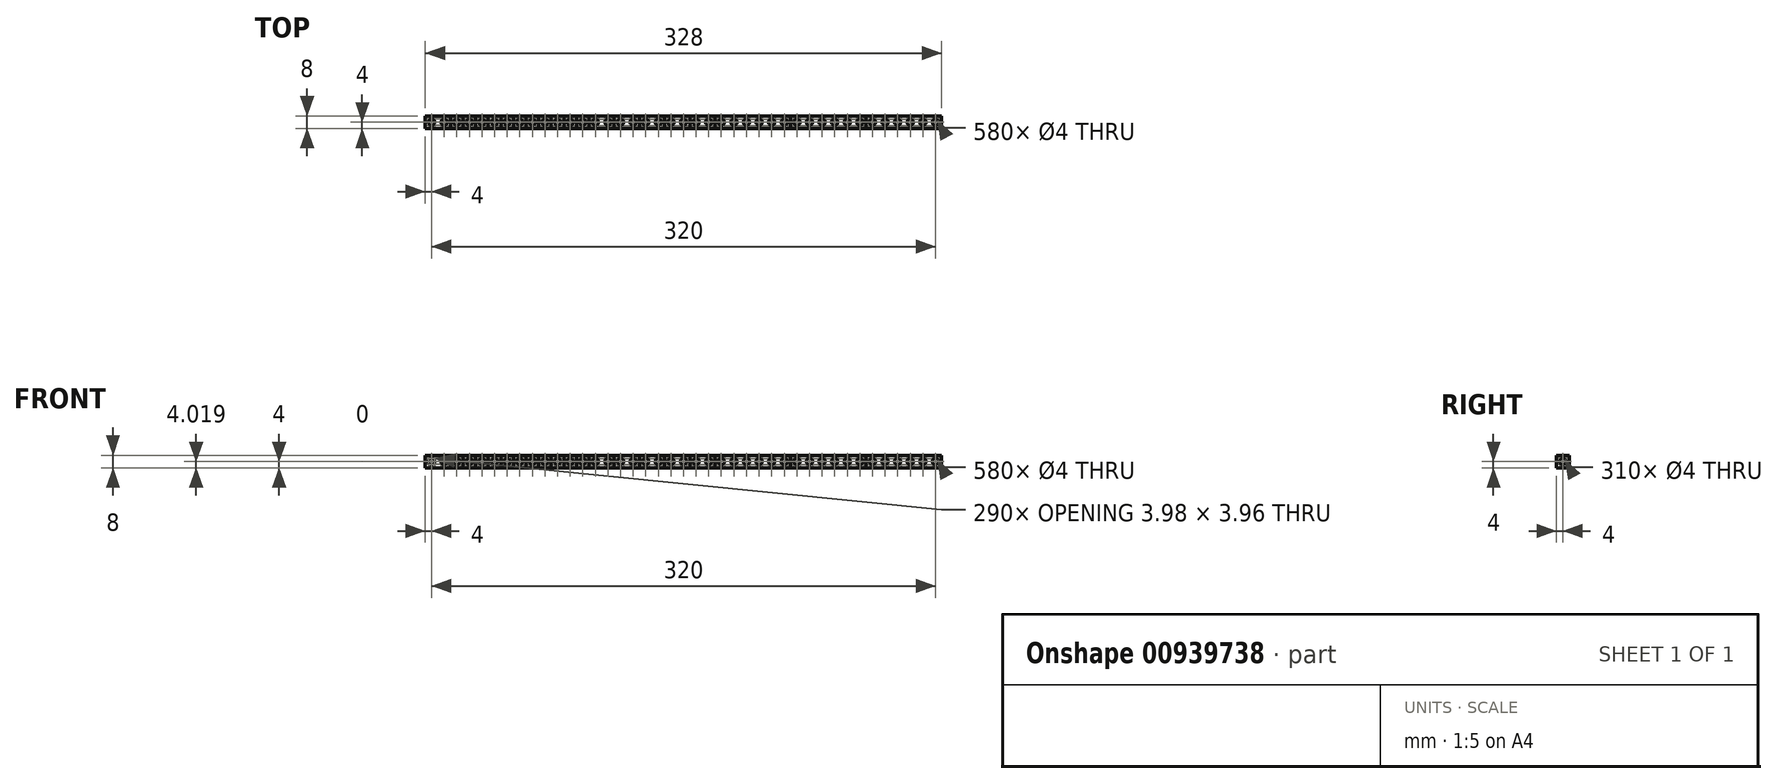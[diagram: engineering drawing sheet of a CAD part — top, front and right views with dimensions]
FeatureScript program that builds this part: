
annotation { "Feature Type Name" : "Feature", "Feature Type Description" : "" }
export const myFeature = defineFeature(function(context is Context, id is Id, definition is map)
    precondition{}
    {
        {
            var Q0;
            Q0=qCreatedBy(makeId("Right.planeOp"),FACE);
            var sketch = newSketch(context, id + "F0", { "sketchPlane" : qUnion([Q0])});
            skLineSegment(sketch, "E0.bottom", {"start": v(4, 4) * mm, "end": v(-4, 4) * mm});
            skLineSegment(sketch, "E0.top", {"start": v(4, -4) * mm, "end": v(-4, -4) * mm});
            skLineSegment(sketch, "E0.left", {"start": v(4, 4) * mm, "end": v(4, -4) * mm});
            skLineSegment(sketch, "E0.right", {"start": v(-4, 4) * mm, "end": v(-4, -4) * mm});
            skPoint(sketch, "E0.middle", {"position": v(0, 0) * mm});
            skSolve(sketch);
        }
        {
            var Q0;
            Q0=qSketchRegion(id+"F0",true);
            extrude(context, id + "F1", {"entities" : qUnion([Q0]), "depth" : 16 * mm, "offsetDistance" : 25 * mm});
        }
        {
            var Q0;
            Q0=qSketchRegion(id+"F0",true);
            extrude(context, id + "F2", {"entities" : qUnion([Q0]), "depth" : 24 * mm, "offsetDistance" : 25 * mm});
        }
        {
            var Q0;
            Q0=qSketchRegion(id+"F0",true);
            extrude(context, id + "F3", {"entities" : qUnion([Q0]), "depth" : 32 * mm, "offsetDistance" : 25 * mm});
        }
        {
            var Q0;
            Q0=qSketchRegion(id+"F0",true);
            extrude(context, id + "F4", {"entities" : qUnion([Q0]), "depth" : 40 * mm, "offsetDistance" : 25 * mm});
        }
        {
            var Q0;
            Q0=qSketchRegion(id+"F0",true);
            extrude(context, id + "F5", {"entities" : qUnion([Q0]), "depth" : 48 * mm, "offsetDistance" : 25 * mm});
        }
        {
            var Q0;
            Q0=qSketchRegion(id+"F0",true);
            extrude(context, id + "F6", {"entities" : qUnion([Q0]), "depth" : 56 * mm, "offsetDistance" : 25 * mm});
        }
        {
            var Q0;
            Q0=qSketchRegion(id+"F0",true);
            extrude(context, id + "F7", {"entities" : qUnion([Q0]), "depth" : 64 * mm, "offsetDistance" : 25 * mm});
        }
        {
            var Q0;
            Q0=qSketchRegion(id+"F0",true);
            extrude(context, id + "F8", {"entities" : qUnion([Q0]), "depth" : 72 * mm, "offsetDistance" : 25 * mm});
        }
        {
            var Q0;
            Q0=qSketchRegion(id+"F0",true);
            extrude(context, id + "F9", {"entities" : qUnion([Q0]), "depth" : 80 * mm, "offsetDistance" : 25 * mm});
        }
        {
            var Q0;
            Q0=qSketchRegion(id+"F0",true);
            extrude(context, id + "F10", {"entities" : qUnion([Q0]), "depth" : 88 * mm, "offsetDistance" : 25 * mm});
        }
        {
            var Q0;
            Q0=qSketchRegion(id+"F0",true);
            extrude(context, id + "F11", {"entities" : qUnion([Q0]), "depth" : 96 * mm, "offsetDistance" : 25 * mm});
        }
        {
            var Q0;
            Q0=qSketchRegion(id+"F0",true);
            extrude(context, id + "F12", {"entities" : qUnion([Q0]), "depth" : 104 * mm, "offsetDistance" : 25 * mm});
        }
        {
            var Q0;
            Q0=qSketchRegion(id+"F0",true);
            extrude(context, id + "F13", {"entities" : qUnion([Q0]), "depth" : 120 * mm, "offsetDistance" : 25 * mm});
        }
        {
            var Q0;
            Q0=qSketchRegion(id+"F0",true);
            extrude(context, id + "F14", {"entities" : qUnion([Q0]), "depth" : 136 * mm, "offsetDistance" : 25 * mm});
        }
        {
            var Q0;
            Q0=qSketchRegion(id+"F0",true);
            extrude(context, id + "F15", {"entities" : qUnion([Q0]), "depth" : 152 * mm, "offsetDistance" : 25 * mm});
        }
        {
            var Q0;
            Q0=qSketchRegion(id+"F0",true);
            extrude(context, id + "F16", {"entities" : qUnion([Q0]), "depth" : 168 * mm, "offsetDistance" : 25 * mm});
        }
        {
            var Q0;
            Q0=qSketchRegion(id+"F0",true);
            extrude(context, id + "F17", {"entities" : qUnion([Q0]), "depth" : 184 * mm, "offsetDistance" : 25 * mm});
        }
        {
            var Q0;
            Q0=qSketchRegion(id+"F0",true);
            extrude(context, id + "F18", {"entities" : qUnion([Q0]), "depth" : 232 * mm, "offsetDistance" : 25 * mm});
        }
        {
            var Q0;
            Q0=qSketchRegion(id+"F0",true);
            extrude(context, id + "F19", {"entities" : qUnion([Q0]), "depth" : 280 * mm, "offsetDistance" : 25 * mm});
        }
        {
            var Q0;
            Q0=qSketchRegion(id+"F0",true);
            extrude(context, id + "F20", {"entities" : qUnion([Q0]), "depth" : 328 * mm, "offsetDistance" : 25 * mm});
        }
        {
            var Q0;
            Q0=qCreatedBy(makeId("Front.planeOp"),FACE);
            var sketch = newSketch(context, id + "F21", { "sketchPlane" : qUnion([Q0])});
            skCircle(sketch, "E1", {"center": v(4, 0) * mm, "radius": 2 * mm});
            skCircle(sketch, "E2.1.0.0", {"center": v(12, 0) * mm, "radius": 2 * mm});
            skCircle(sketch, "E2.2.0.0", {"center": v(20, 0) * mm, "radius": 2 * mm});
            skCircle(sketch, "E2.3.0.0", {"center": v(28, 0) * mm, "radius": 2 * mm});
            skCircle(sketch, "E2.4.0.0", {"center": v(36, 0) * mm, "radius": 2 * mm});
            skCircle(sketch, "E2.5.0.0", {"center": v(44, 0) * mm, "radius": 2 * mm});
            skCircle(sketch, "E2.6.0.0", {"center": v(52, 0) * mm, "radius": 2 * mm});
            skCircle(sketch, "E2.7.0.0", {"center": v(60, 0) * mm, "radius": 2 * mm});
            skCircle(sketch, "E2.8.0.0", {"center": v(68, 0) * mm, "radius": 2 * mm});
            skCircle(sketch, "E2.9.0.0", {"center": v(76, 0) * mm, "radius": 2 * mm});
            skCircle(sketch, "E2.10.0.0", {"center": v(84, 0) * mm, "radius": 2 * mm});
            skCircle(sketch, "E2.11.0.0", {"center": v(92, 0) * mm, "radius": 2 * mm});
            skCircle(sketch, "E2.12.0.0", {"center": v(100, 0) * mm, "radius": 2 * mm});
            skCircle(sketch, "E2.13.0.0", {"center": v(108, 0) * mm, "radius": 2 * mm});
            skCircle(sketch, "E2.14.0.0", {"center": v(116, 0) * mm, "radius": 2 * mm});
            skCircle(sketch, "E2.15.0.0", {"center": v(124, 0) * mm, "radius": 2 * mm});
            skCircle(sketch, "E2.16.0.0", {"center": v(132, 0) * mm, "radius": 2 * mm});
            skCircle(sketch, "E2.17.0.0", {"center": v(140, 0) * mm, "radius": 2 * mm});
            skCircle(sketch, "E2.18.0.0", {"center": v(148, 0) * mm, "radius": 2 * mm});
            skCircle(sketch, "E2.19.0.0", {"center": v(156, 0) * mm, "radius": 2 * mm});
            skCircle(sketch, "E2.20.0.0", {"center": v(164, 0) * mm, "radius": 2 * mm});
            skCircle(sketch, "E2.21.0.0", {"center": v(172, 0) * mm, "radius": 2 * mm});
            skCircle(sketch, "E2.22.0.0", {"center": v(180, 0) * mm, "radius": 2 * mm});
            skCircle(sketch, "E2.23.0.0", {"center": v(188, 0) * mm, "radius": 2 * mm});
            skCircle(sketch, "E2.24.0.0", {"center": v(196, 0) * mm, "radius": 2 * mm});
            skCircle(sketch, "E2.25.0.0", {"center": v(204, 0) * mm, "radius": 2 * mm});
            skCircle(sketch, "E2.26.0.0", {"center": v(212, 0) * mm, "radius": 2 * mm});
            skCircle(sketch, "E2.27.0.0", {"center": v(220, 0) * mm, "radius": 2 * mm});
            skCircle(sketch, "E2.28.0.0", {"center": v(228, 0) * mm, "radius": 2 * mm});
            skCircle(sketch, "E2.29.0.0", {"center": v(236, 0) * mm, "radius": 2 * mm});
            skCircle(sketch, "E2.30.0.0", {"center": v(244, 0) * mm, "radius": 2 * mm});
            skCircle(sketch, "E2.31.0.0", {"center": v(252, 0) * mm, "radius": 2 * mm});
            skCircle(sketch, "E2.32.0.0", {"center": v(260, 0) * mm, "radius": 2 * mm});
            skCircle(sketch, "E2.33.0.0", {"center": v(268, 0) * mm, "radius": 2 * mm});
            skCircle(sketch, "E2.34.0.0", {"center": v(276, 0) * mm, "radius": 2 * mm});
            skCircle(sketch, "E2.35.0.0", {"center": v(284, 0) * mm, "radius": 2 * mm});
            skCircle(sketch, "E2.36.0.0", {"center": v(292, 0) * mm, "radius": 2 * mm});
            skCircle(sketch, "E2.37.0.0", {"center": v(300, 0) * mm, "radius": 2 * mm});
            skCircle(sketch, "E2.38.0.0", {"center": v(308, 0) * mm, "radius": 2 * mm});
            skCircle(sketch, "E2.39.0.0", {"center": v(316, 0) * mm, "radius": 2 * mm});
            skCircle(sketch, "E2.40.0.0", {"center": v(324, 0) * mm, "radius": 2 * mm});
            skLineSegment(sketch, "E2.direction1", {"start": v(4, 0) * mm, "end": v(12, 0) * mm, "construction": true});
            skSolve(sketch);
        }
        {
            var Q0;
            Q0=qSketchRegion(id+"F21",true);
            extrude(context, id + "F22", {"entities" : qUnion([Q0]), "operationType" : NewBodyOperationType.REMOVE, "oppositeDirection" : true, "depth" : 25 * mm, "offsetDistance" : 25 * mm, "symmetric" : true});
        }
        {
            var Q0;
            Q0=qCreatedBy(makeId("Top.planeOp"),FACE);
            var sketch = newSketch(context, id + "F23", { "sketchPlane" : qUnion([Q0])});
            skCircle(sketch, "E3", {"center": v(4, 0) * mm, "radius": 2 * mm});
            skCircle(sketch, "E4.1.0.0", {"center": v(12, 0) * mm, "radius": 2 * mm});
            skCircle(sketch, "E4.2.0.0", {"center": v(20, 0) * mm, "radius": 2 * mm});
            skCircle(sketch, "E4.3.0.0", {"center": v(28, 0) * mm, "radius": 2 * mm});
            skCircle(sketch, "E4.4.0.0", {"center": v(36, 0) * mm, "radius": 2 * mm});
            skCircle(sketch, "E4.5.0.0", {"center": v(44, 0) * mm, "radius": 2 * mm});
            skCircle(sketch, "E4.6.0.0", {"center": v(52, 0) * mm, "radius": 2 * mm});
            skCircle(sketch, "E4.7.0.0", {"center": v(60, 0) * mm, "radius": 2 * mm});
            skCircle(sketch, "E4.8.0.0", {"center": v(68, 0) * mm, "radius": 2 * mm});
            skCircle(sketch, "E4.9.0.0", {"center": v(76, 0) * mm, "radius": 2 * mm});
            skCircle(sketch, "E4.10.0.0", {"center": v(84, 0) * mm, "radius": 2 * mm});
            skCircle(sketch, "E4.11.0.0", {"center": v(92, 0) * mm, "radius": 2 * mm});
            skCircle(sketch, "E4.12.0.0", {"center": v(100, 0) * mm, "radius": 2 * mm});
            skCircle(sketch, "E4.13.0.0", {"center": v(108, 0) * mm, "radius": 2 * mm});
            skCircle(sketch, "E4.14.0.0", {"center": v(116, 0) * mm, "radius": 2 * mm});
            skCircle(sketch, "E4.15.0.0", {"center": v(124, 0) * mm, "radius": 2 * mm});
            skCircle(sketch, "E4.16.0.0", {"center": v(132, 0) * mm, "radius": 2 * mm});
            skCircle(sketch, "E4.17.0.0", {"center": v(140, 0) * mm, "radius": 2 * mm});
            skCircle(sketch, "E4.18.0.0", {"center": v(148, 0) * mm, "radius": 2 * mm});
            skCircle(sketch, "E4.19.0.0", {"center": v(156, 0) * mm, "radius": 2 * mm});
            skCircle(sketch, "E4.20.0.0", {"center": v(164, 0) * mm, "radius": 2 * mm});
            skCircle(sketch, "E4.21.0.0", {"center": v(172, 0) * mm, "radius": 2 * mm});
            skCircle(sketch, "E4.22.0.0", {"center": v(180, 0) * mm, "radius": 2 * mm});
            skCircle(sketch, "E4.23.0.0", {"center": v(188, 0) * mm, "radius": 2 * mm});
            skCircle(sketch, "E4.24.0.0", {"center": v(196, 0) * mm, "radius": 2 * mm});
            skCircle(sketch, "E4.25.0.0", {"center": v(204, 0) * mm, "radius": 2 * mm});
            skCircle(sketch, "E4.26.0.0", {"center": v(212, 0) * mm, "radius": 2 * mm});
            skCircle(sketch, "E4.27.0.0", {"center": v(220, 0) * mm, "radius": 2 * mm});
            skCircle(sketch, "E4.28.0.0", {"center": v(228, 0) * mm, "radius": 2 * mm});
            skCircle(sketch, "E4.29.0.0", {"center": v(236, 0) * mm, "radius": 2 * mm});
            skCircle(sketch, "E4.30.0.0", {"center": v(244, 0) * mm, "radius": 2 * mm});
            skCircle(sketch, "E4.31.0.0", {"center": v(252, 0) * mm, "radius": 2 * mm});
            skCircle(sketch, "E4.32.0.0", {"center": v(260, 0) * mm, "radius": 2 * mm});
            skCircle(sketch, "E4.33.0.0", {"center": v(268, 0) * mm, "radius": 2 * mm});
            skCircle(sketch, "E4.34.0.0", {"center": v(276, 0) * mm, "radius": 2 * mm});
            skCircle(sketch, "E4.35.0.0", {"center": v(284, 0) * mm, "radius": 2 * mm});
            skCircle(sketch, "E4.36.0.0", {"center": v(292, 0) * mm, "radius": 2 * mm});
            skCircle(sketch, "E4.37.0.0", {"center": v(300, 0) * mm, "radius": 2 * mm});
            skCircle(sketch, "E4.38.0.0", {"center": v(308, 0) * mm, "radius": 2 * mm});
            skCircle(sketch, "E4.39.0.0", {"center": v(316, 0) * mm, "radius": 2 * mm});
            skCircle(sketch, "E4.40.0.0", {"center": v(324, 0) * mm, "radius": 2 * mm});
            skLineSegment(sketch, "E4.direction1", {"start": v(4, 0) * mm, "end": v(12, 0) * mm, "construction": true});
            skSolve(sketch);
        }
        {
            var Q0;
            Q0=qSketchRegion(id+"F23",true);
            extrude(context, id + "F24", {"entities" : qUnion([Q0]), "operationType" : NewBodyOperationType.REMOVE, "depth" : 25 * mm, "offsetDistance" : 25 * mm, "symmetric" : true});
        }
        {
            var Q0;
            Q0=qCreatedBy(makeId("Right.planeOp"),FACE);
            var sketch = newSketch(context, id + "F25", { "sketchPlane" : qUnion([Q0])});
            skCircle(sketch, "E5", {"center": v(0, 0) * mm, "radius": 2 * mm});
            skSolve(sketch);
        }
        {
            var Q0;
            Q0=qSketchRegion(id+"F25",true);
            extrude(context, id + "F26", {"entities" : qUnion([Q0]), "operationType" : NewBodyOperationType.REMOVE, "depth" : 12 * mm, "offsetDistance" : 25 * mm});
        }
        {
            var Q0;
            Q0=qCreatedBy(makeId("Right.planeOp"),FACE);
            cPlane(context, id + "F27", {"entities" : qUnion([Q0]), "cplaneType" : CPlaneType.OFFSET, "offset" : 328 * mm, "width" : 150 * mm, "height" : 150 * mm});
        }
        {
            var Q0;
            Q0=qCreatedBy(id+"F27.planeOp",FACE);
            var sketch = newSketch(context, id + "F28", { "sketchPlane" : qUnion([Q0])});
            skCircle(sketch, "E6", {"center": v(0, 0) * mm, "radius": 2 * mm});
            skSolve(sketch);
        }
        {
            var Q0;
            Q0=qSketchRegion(id+"F28",true);
            var Q1;
            {var subQ0=makeQuery(id+"F24.opExtrude","SWEPT_FACE",FACE,{"disambiguationData":[OSD([sQuery(id+"F23.wireOp",EDGE,"E4.1.0.0")])]});Q1=makeQuery(id+"F24.boolean.opBoolean","COPY",FACE,{"disambiguationData":[TD([makeQuery(id+"F1.opExtrude","SWEPT_FACE",FACE,{"disambiguationData":[OSD([sQuery(id+"F0.wireOp",EDGE,"E0.top")])]})])],"derivedFrom":subQ0});}
            extrude(context, id + "F29", {"entities" : qUnion([Q0]), "operationType" : NewBodyOperationType.REMOVE, "endBound" : BoundingType.UP_TO_SURFACE, "oppositeDirection" : true, "depth" : 25 * mm, "endBoundEntityFace" : qUnion([Q1]), "offsetDistance" : 25 * mm});
        }
        {
            var Q0;
            Q0=qSketchRegion(id+"F28",true);
            var Q1;
            {var subQ0=makeQuery(id+"F24.opExtrude","SWEPT_FACE",FACE,{"disambiguationData":[OSD([sQuery(id+"F23.wireOp",EDGE,"E4.1.0.0")])]});Q1=makeQuery(id+"F24.boolean.opBoolean","COPY",FACE,{"disambiguationData":[TD([makeQuery(id+"F1.opExtrude","SWEPT_FACE",FACE,{"disambiguationData":[OSD([sQuery(id+"F0.wireOp",EDGE,"E0.top")])]})])],"derivedFrom":subQ0});}
            extrude(context, id + "F30", {"entities" : qUnion([Q0]), "operationType" : NewBodyOperationType.REMOVE, "endBound" : BoundingType.UP_TO_SURFACE, "oppositeDirection" : true, "depth" : 25 * mm, "endBoundEntityFace" : qUnion([Q1]), "offsetDistance" : 25 * mm});
        }
        {
            var Q0;
            Q0=qSketchRegion(id+"F28",true);
            var Q1;
            {var subQ0=makeQuery(id+"F24.opExtrude","SWEPT_FACE",FACE,{"disambiguationData":[OSD([sQuery(id+"F23.wireOp",EDGE,"E4.2.0.0")])]});Q1=makeQuery(id+"F24.boolean.opBoolean","COPY",FACE,{"disambiguationData":[TD([makeQuery(id+"F2.opExtrude","SWEPT_FACE",FACE,{"disambiguationData":[OSD([sQuery(id+"F0.wireOp",EDGE,"E0.top")])]})])],"derivedFrom":subQ0});}
            extrude(context, id + "F31", {"entities" : qUnion([Q0]), "operationType" : NewBodyOperationType.REMOVE, "endBound" : BoundingType.UP_TO_SURFACE, "oppositeDirection" : true, "depth" : 25 * mm, "endBoundEntityFace" : qUnion([Q1]), "offsetDistance" : 25 * mm});
        }
        {
            var Q0;
            Q0=qSketchRegion(id+"F28",true);
            var Q1;
            {var subQ0=makeQuery(id+"F24.opExtrude","SWEPT_FACE",FACE,{"disambiguationData":[OSD([sQuery(id+"F23.wireOp",EDGE,"E4.3.0.0")])]});Q1=makeQuery(id+"F24.boolean.opBoolean","COPY",FACE,{"disambiguationData":[TD([makeQuery(id+"F3.opExtrude","SWEPT_FACE",FACE,{"disambiguationData":[OSD([sQuery(id+"F0.wireOp",EDGE,"E0.top")])]})])],"derivedFrom":subQ0});}
            extrude(context, id + "F32", {"entities" : qUnion([Q0]), "operationType" : NewBodyOperationType.REMOVE, "endBound" : BoundingType.UP_TO_SURFACE, "oppositeDirection" : true, "depth" : 25 * mm, "endBoundEntityFace" : qUnion([Q1]), "offsetDistance" : 25 * mm});
        }
        {
            var Q0;
            Q0=qSketchRegion(id+"F28",true);
            var Q1;
            {var subQ0=makeQuery(id+"F24.opExtrude","SWEPT_FACE",FACE,{"disambiguationData":[OSD([sQuery(id+"F23.wireOp",EDGE,"E4.4.0.0")])]});Q1=makeQuery(id+"F24.boolean.opBoolean","COPY",FACE,{"disambiguationData":[TD([makeQuery(id+"F5.opExtrude","SWEPT_FACE",FACE,{"disambiguationData":[OSD([sQuery(id+"F0.wireOp",EDGE,"E0.top")])]})])],"derivedFrom":subQ0});}
            extrude(context, id + "F33", {"entities" : qUnion([Q0]), "operationType" : NewBodyOperationType.REMOVE, "endBound" : BoundingType.UP_TO_SURFACE, "oppositeDirection" : true, "depth" : 25 * mm, "endBoundEntityFace" : qUnion([Q1]), "offsetDistance" : 25 * mm});
        }
        {
            var Q0;
            Q0=qSketchRegion(id+"F28",true);
            var Q1;
            {var subQ0=makeQuery(id+"F24.opExtrude","SWEPT_FACE",FACE,{"disambiguationData":[OSD([sQuery(id+"F23.wireOp",EDGE,"E4.5.0.0")])]});Q1=makeQuery(id+"F24.boolean.opBoolean","COPY",FACE,{"disambiguationData":[TD([makeQuery(id+"F6.opExtrude","SWEPT_FACE",FACE,{"disambiguationData":[OSD([sQuery(id+"F0.wireOp",EDGE,"E0.top")])]})])],"derivedFrom":subQ0});}
            extrude(context, id + "F34", {"entities" : qUnion([Q0]), "operationType" : NewBodyOperationType.REMOVE, "endBound" : BoundingType.UP_TO_SURFACE, "oppositeDirection" : true, "depth" : 25 * mm, "endBoundEntityFace" : qUnion([Q1]), "offsetDistance" : 25 * mm});
        }
        {
            var Q0;
            Q0=qSketchRegion(id+"F28",true);
            var Q1;
            {var subQ0=makeQuery(id+"F24.opExtrude","SWEPT_FACE",FACE,{"disambiguationData":[OSD([sQuery(id+"F23.wireOp",EDGE,"E4.6.0.0")])]});Q1=makeQuery(id+"F24.boolean.opBoolean","COPY",FACE,{"disambiguationData":[TD([makeQuery(id+"F7.opExtrude","SWEPT_FACE",FACE,{"disambiguationData":[OSD([sQuery(id+"F0.wireOp",EDGE,"E0.top")])]})])],"derivedFrom":subQ0});}
            extrude(context, id + "F35", {"entities" : qUnion([Q0]), "operationType" : NewBodyOperationType.REMOVE, "endBound" : BoundingType.UP_TO_SURFACE, "oppositeDirection" : true, "depth" : 25 * mm, "endBoundEntityFace" : qUnion([Q1]), "offsetDistance" : 25 * mm});
        }
        {
            var Q0;
            Q0=qSketchRegion(id+"F28",true);
            var Q1;
            {var subQ0=makeQuery(id+"F24.opExtrude","SWEPT_FACE",FACE,{"disambiguationData":[OSD([sQuery(id+"F23.wireOp",EDGE,"E4.7.0.0")])]});Q1=makeQuery(id+"F24.boolean.opBoolean","COPY",FACE,{"disambiguationData":[TD([makeQuery(id+"F8.opExtrude","SWEPT_FACE",FACE,{"disambiguationData":[OSD([sQuery(id+"F0.wireOp",EDGE,"E0.top")])]})])],"derivedFrom":subQ0});}
            extrude(context, id + "F36", {"entities" : qUnion([Q0]), "operationType" : NewBodyOperationType.REMOVE, "endBound" : BoundingType.UP_TO_SURFACE, "oppositeDirection" : true, "depth" : 25 * mm, "endBoundEntityFace" : qUnion([Q1]), "offsetDistance" : 25 * mm});
        }
        {
            var Q0;
            Q0=qSketchRegion(id+"F28",true);
            var Q1;
            {var subQ0=makeQuery(id+"F24.opExtrude","SWEPT_FACE",FACE,{"disambiguationData":[OSD([sQuery(id+"F23.wireOp",EDGE,"E4.8.0.0")])]});Q1=makeQuery(id+"F24.boolean.opBoolean","COPY",FACE,{"disambiguationData":[TD([makeQuery(id+"F9.opExtrude","SWEPT_FACE",FACE,{"disambiguationData":[OSD([sQuery(id+"F0.wireOp",EDGE,"E0.top")])]})])],"derivedFrom":subQ0});}
            extrude(context, id + "F37", {"entities" : qUnion([Q0]), "operationType" : NewBodyOperationType.REMOVE, "endBound" : BoundingType.UP_TO_SURFACE, "oppositeDirection" : true, "depth" : 25 * mm, "endBoundEntityFace" : qUnion([Q1]), "offsetDistance" : 25 * mm});
        }
        {
            var Q0;
            Q0=qSketchRegion(id+"F28",true);
            var Q1;
            {var subQ0=makeQuery(id+"F24.opExtrude","SWEPT_FACE",FACE,{"disambiguationData":[OSD([sQuery(id+"F23.wireOp",EDGE,"E4.9.0.0")])]});Q1=makeQuery(id+"F24.boolean.opBoolean","COPY",FACE,{"disambiguationData":[TD([makeQuery(id+"F10.opExtrude","SWEPT_FACE",FACE,{"disambiguationData":[OSD([sQuery(id+"F0.wireOp",EDGE,"E0.top")])]})])],"derivedFrom":subQ0});}
            extrude(context, id + "F38", {"entities" : qUnion([Q0]), "operationType" : NewBodyOperationType.REMOVE, "endBound" : BoundingType.UP_TO_SURFACE, "oppositeDirection" : true, "depth" : 25 * mm, "endBoundEntityFace" : qUnion([Q1]), "offsetDistance" : 25 * mm});
        }
        {
            var Q0;
            Q0=qSketchRegion(id+"F28",true);
            var Q1;
            {var subQ0=makeQuery(id+"F24.opExtrude","SWEPT_FACE",FACE,{"disambiguationData":[OSD([sQuery(id+"F23.wireOp",EDGE,"E4.10.0.0")])]});Q1=makeQuery(id+"F24.boolean.opBoolean","COPY",FACE,{"disambiguationData":[TD([makeQuery(id+"F11.opExtrude","SWEPT_FACE",FACE,{"disambiguationData":[OSD([sQuery(id+"F0.wireOp",EDGE,"E0.top")])]})])],"derivedFrom":subQ0});}
            extrude(context, id + "F39", {"entities" : qUnion([Q0]), "operationType" : NewBodyOperationType.REMOVE, "endBound" : BoundingType.UP_TO_SURFACE, "oppositeDirection" : true, "depth" : 25 * mm, "endBoundEntityFace" : qUnion([Q1]), "offsetDistance" : 25 * mm});
        }
        {
            var Q0;
            Q0=qSketchRegion(id+"F28",true);
            var Q1;
            {var subQ0=makeQuery(id+"F24.opExtrude","SWEPT_FACE",FACE,{"disambiguationData":[OSD([sQuery(id+"F23.wireOp",EDGE,"E4.11.0.0")])]});Q1=makeQuery(id+"F24.boolean.opBoolean","COPY",FACE,{"disambiguationData":[TD([makeQuery(id+"F12.opExtrude","SWEPT_FACE",FACE,{"disambiguationData":[OSD([sQuery(id+"F0.wireOp",EDGE,"E0.top")])]})])],"derivedFrom":subQ0});}
            extrude(context, id + "F40", {"entities" : qUnion([Q0]), "operationType" : NewBodyOperationType.REMOVE, "endBound" : BoundingType.UP_TO_SURFACE, "oppositeDirection" : true, "depth" : 25 * mm, "endBoundEntityFace" : qUnion([Q1]), "offsetDistance" : 25 * mm});
        }
        {
            var Q0;
            Q0=qSketchRegion(id+"F28",true);
            var Q1;
            {var subQ0=makeQuery(id+"F24.opExtrude","SWEPT_FACE",FACE,{"disambiguationData":[OSD([sQuery(id+"F23.wireOp",EDGE,"E4.13.0.0")])]});Q1=makeQuery(id+"F24.boolean.opBoolean","COPY",FACE,{"disambiguationData":[TD([makeQuery(id+"F13.opExtrude","SWEPT_FACE",FACE,{"disambiguationData":[OSD([sQuery(id+"F0.wireOp",EDGE,"E0.top")])]})])],"derivedFrom":subQ0});}
            extrude(context, id + "F41", {"entities" : qUnion([Q0]), "operationType" : NewBodyOperationType.REMOVE, "endBound" : BoundingType.UP_TO_SURFACE, "oppositeDirection" : true, "depth" : 25 * mm, "endBoundEntityFace" : qUnion([Q1]), "offsetDistance" : 25 * mm});
        }
        {
            var Q0;
            Q0=qSketchRegion(id+"F28",true);
            var Q1;
            {var subQ0=makeQuery(id+"F24.opExtrude","SWEPT_FACE",FACE,{"disambiguationData":[OSD([sQuery(id+"F23.wireOp",EDGE,"E4.15.0.0")])]});Q1=makeQuery(id+"F24.boolean.opBoolean","COPY",FACE,{"disambiguationData":[TD([makeQuery(id+"F14.opExtrude","SWEPT_FACE",FACE,{"disambiguationData":[OSD([sQuery(id+"F0.wireOp",EDGE,"E0.top")])]})])],"derivedFrom":subQ0});}
            extrude(context, id + "F42", {"entities" : qUnion([Q0]), "operationType" : NewBodyOperationType.REMOVE, "endBound" : BoundingType.UP_TO_SURFACE, "oppositeDirection" : true, "depth" : 25 * mm, "endBoundEntityFace" : qUnion([Q1]), "offsetDistance" : 25 * mm});
        }
        {
            var Q0;
            Q0=qSketchRegion(id+"F28",true);
            var Q1;
            {var subQ0=makeQuery(id+"F24.opExtrude","SWEPT_FACE",FACE,{"disambiguationData":[OSD([sQuery(id+"F23.wireOp",EDGE,"E4.17.0.0")])]});Q1=makeQuery(id+"F24.boolean.opBoolean","COPY",FACE,{"disambiguationData":[TD([makeQuery(id+"F15.opExtrude","SWEPT_FACE",FACE,{"disambiguationData":[OSD([sQuery(id+"F0.wireOp",EDGE,"E0.top")])]})])],"derivedFrom":subQ0});}
            extrude(context, id + "F43", {"entities" : qUnion([Q0]), "operationType" : NewBodyOperationType.REMOVE, "endBound" : BoundingType.UP_TO_SURFACE, "oppositeDirection" : true, "depth" : 25 * mm, "endBoundEntityFace" : qUnion([Q1]), "offsetDistance" : 25 * mm});
        }
        {
            var Q0;
            Q0=qSketchRegion(id+"F28",true);
            var Q1;
            {var subQ0=makeQuery(id+"F24.opExtrude","SWEPT_FACE",FACE,{"disambiguationData":[OSD([sQuery(id+"F23.wireOp",EDGE,"E4.19.0.0")])]});Q1=makeQuery(id+"F24.boolean.opBoolean","COPY",FACE,{"disambiguationData":[TD([makeQuery(id+"F16.opExtrude","SWEPT_FACE",FACE,{"disambiguationData":[OSD([sQuery(id+"F0.wireOp",EDGE,"E0.top")])]})])],"derivedFrom":subQ0});}
            extrude(context, id + "F44", {"entities" : qUnion([Q0]), "operationType" : NewBodyOperationType.REMOVE, "endBound" : BoundingType.UP_TO_SURFACE, "oppositeDirection" : true, "depth" : 25 * mm, "endBoundEntityFace" : qUnion([Q1]), "offsetDistance" : 25 * mm});
        }
        {
            var Q0;
            Q0=qSketchRegion(id+"F28",true);
            var Q1;
            {var subQ0=makeQuery(id+"F24.opExtrude","SWEPT_FACE",FACE,{"disambiguationData":[OSD([sQuery(id+"F23.wireOp",EDGE,"E4.21.0.0")])]});Q1=makeQuery(id+"F24.boolean.opBoolean","COPY",FACE,{"disambiguationData":[TD([makeQuery(id+"F17.opExtrude","SWEPT_FACE",FACE,{"disambiguationData":[OSD([sQuery(id+"F0.wireOp",EDGE,"E0.top")])]})])],"derivedFrom":subQ0});}
            extrude(context, id + "F45", {"entities" : qUnion([Q0]), "operationType" : NewBodyOperationType.REMOVE, "endBound" : BoundingType.UP_TO_SURFACE, "oppositeDirection" : true, "depth" : 25 * mm, "endBoundEntityFace" : qUnion([Q1]), "offsetDistance" : 25 * mm});
        }
        {
            var Q0;
            Q0=qSketchRegion(id+"F28",true);
            var Q1;
            {var subQ0=makeQuery(id+"F24.opExtrude","SWEPT_FACE",FACE,{"disambiguationData":[OSD([sQuery(id+"F23.wireOp",EDGE,"E4.27.0.0")])]});Q1=makeQuery(id+"F24.boolean.opBoolean","COPY",FACE,{"disambiguationData":[TD([makeQuery(id+"F18.opExtrude","SWEPT_FACE",FACE,{"disambiguationData":[OSD([sQuery(id+"F0.wireOp",EDGE,"E0.top")])]})])],"derivedFrom":subQ0});}
            extrude(context, id + "F46", {"entities" : qUnion([Q0]), "operationType" : NewBodyOperationType.REMOVE, "endBound" : BoundingType.UP_TO_SURFACE, "oppositeDirection" : true, "depth" : 25 * mm, "endBoundEntityFace" : qUnion([Q1]), "offsetDistance" : 25 * mm});
        }
        {
            var Q0;
            Q0=qSketchRegion(id+"F28",true);
            var Q1;
            {var subQ0=makeQuery(id+"F24.opExtrude","SWEPT_FACE",FACE,{"disambiguationData":[OSD([sQuery(id+"F23.wireOp",EDGE,"E4.33.0.0")])]});Q1=makeQuery(id+"F24.boolean.opBoolean","COPY",FACE,{"disambiguationData":[TD([makeQuery(id+"F19.opExtrude","SWEPT_FACE",FACE,{"disambiguationData":[OSD([sQuery(id+"F0.wireOp",EDGE,"E0.top")])]})])],"derivedFrom":subQ0});}
            extrude(context, id + "F47", {"entities" : qUnion([Q0]), "operationType" : NewBodyOperationType.REMOVE, "endBound" : BoundingType.UP_TO_SURFACE, "oppositeDirection" : true, "depth" : 25 * mm, "endBoundEntityFace" : qUnion([Q1]), "offsetDistance" : 25 * mm});
        }
        {
            var Q0;
            Q0=qSketchRegion(id+"F28",true);
            var Q1;
            {var subQ0=makeQuery(id+"F24.opExtrude","SWEPT_FACE",FACE,{"disambiguationData":[OSD([sQuery(id+"F23.wireOp",EDGE,"E4.39.0.0")])]});Q1=makeQuery(id+"F24.boolean.opBoolean","COPY",FACE,{"disambiguationData":[TD([makeQuery(id+"F20.opExtrude","SWEPT_FACE",FACE,{"disambiguationData":[OSD([sQuery(id+"F0.wireOp",EDGE,"E0.top")])]})])],"derivedFrom":subQ0});}
            extrude(context, id + "F48", {"entities" : qUnion([Q0]), "operationType" : NewBodyOperationType.REMOVE, "endBound" : BoundingType.UP_TO_SURFACE, "oppositeDirection" : true, "depth" : 25 * mm, "endBoundEntityFace" : qUnion([Q1]), "offsetDistance" : 25 * mm});
        }
    });
